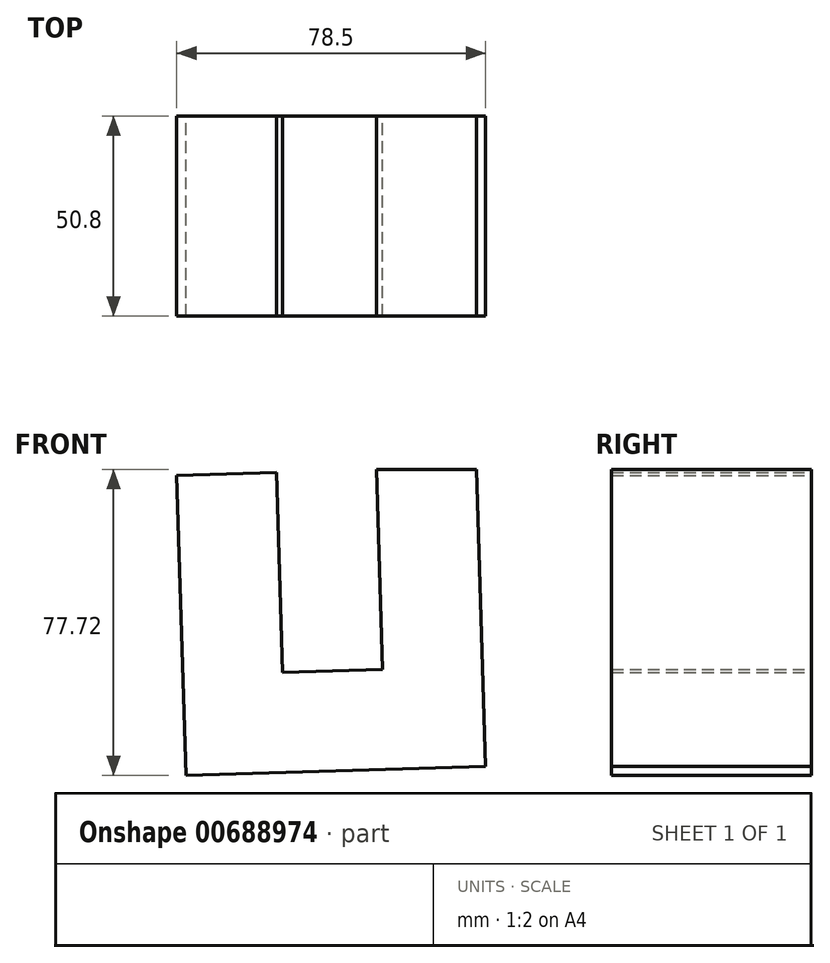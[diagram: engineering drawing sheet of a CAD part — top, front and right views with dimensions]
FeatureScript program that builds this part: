
annotation { "Feature Type Name" : "Feature", "Feature Type Description" : "" }
export const myFeature = defineFeature(function(context is Context, id is Id, definition is map)
    precondition{}
    {
        {
            var Q0;
            Q0=qCreatedBy(makeId("Front.planeOp"),FACE);
            var sketch = newSketch(context, id + "F0", { "sketchPlane" : qUnion([Q0])});
            skLineSegment(sketch, "E0", {"start": v(-56.88, 47.26) * mm, "end": v(-54.54, -28.9) * mm});
            skLineSegment(sketch, "E1", {"start": v(-54.54, -28.9) * mm, "end": v(21.62, -26.57) * mm});
            skLineSegment(sketch, "E2", {"start": v(21.62, -26.57) * mm, "end": v(19.29, 49.6) * mm});
            skLineSegment(sketch, "E3", {"start": v(-56.88, 47.26) * mm, "end": v(-31.49, 48.04) * mm});
            skLineSegment(sketch, "E4", {"start": v(-31.49, 48.04) * mm, "end": v(-29.93, -2.74) * mm});
            skLineSegment(sketch, "E5", {"start": v(-29.93, -2.74) * mm, "end": v(-4.54, -1.96) * mm});
            skLineSegment(sketch, "E6", {"start": v(-4.54, -1.96) * mm, "end": v(-6.09, 48.82) * mm});
            skLineSegment(sketch, "E7", {"start": v(-6.09, 48.82) * mm, "end": v(19.31, 48.82) * mm});
            skSolve(sketch);
        }
        {
            var Q0;
            Q0 = qSketchRegion(id + "F0", true);
            extrude(context, id + "F1", {"entities" : qUnion([Q0]), "depth" : 50.8 * mm, "offsetDistance" : 25.4 * mm});
        }
    });
